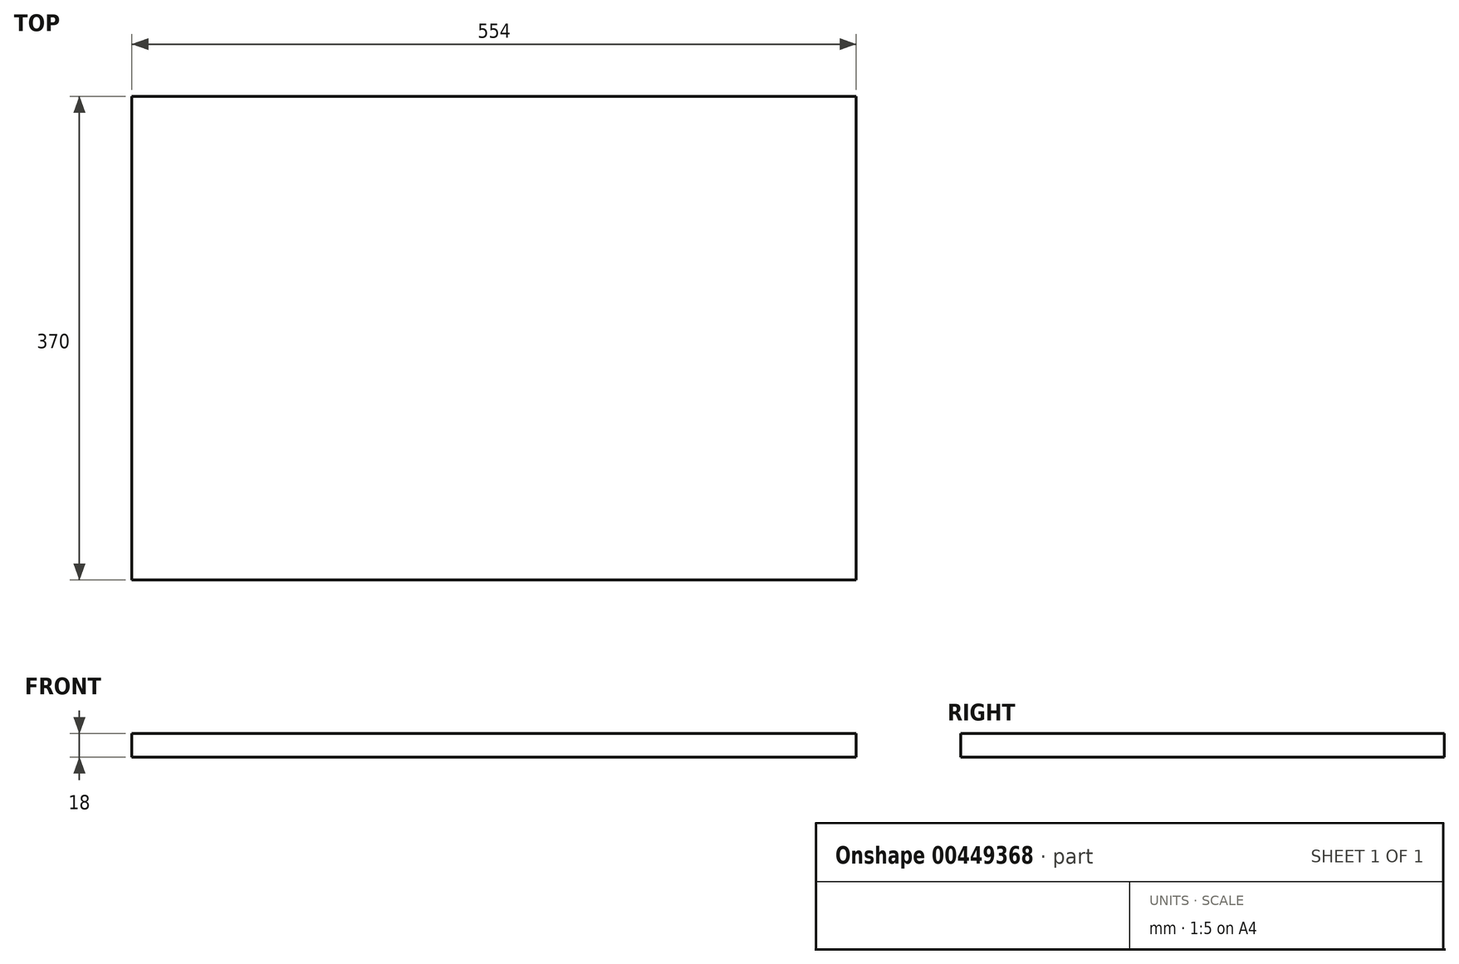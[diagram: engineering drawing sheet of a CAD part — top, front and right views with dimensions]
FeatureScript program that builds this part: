
annotation { "Feature Type Name" : "Feature", "Feature Type Description" : "" }
export const myFeature = defineFeature(function(context is Context, id is Id, definition is map)
    precondition{}
    {
        {
            var Q0;
            Q0=qCreatedBy(makeId("Top.planeOp"),FACE);
            var sketch = newSketch(context, id + "F0", { "sketchPlane" : qUnion([Q0])});
            skLineSegment(sketch, "E0.bottom", {"start": v(0, 0) * mm, "end": v(554, 0) * mm});
            skLineSegment(sketch, "E0.top", {"start": v(0, 370) * mm, "end": v(554, 370) * mm});
            skLineSegment(sketch, "E0.left", {"start": v(0, 0) * mm, "end": v(0, 370) * mm});
            skLineSegment(sketch, "E0.right", {"start": v(554, 0) * mm, "end": v(554, 370) * mm});
            skSolve(sketch);
        }
        {
            var Q0;
            Q0=makeQuery(id+"F0.imprint","IMPRINT",FACE,{"disambiguationData":[TD([[makeQuery(id+"F0.imprint","IMPRINT",EDGE,{"derivedFrom":sQuery(id+"F0.wireOp",EDGE,"E0.bottom")}),1.0]])]});
            extrude(context, id + "F1", {"entities" : qUnion([Q0]), "depth" : 18 * mm, "offsetDistance" : 25 * mm});
        }
    });
